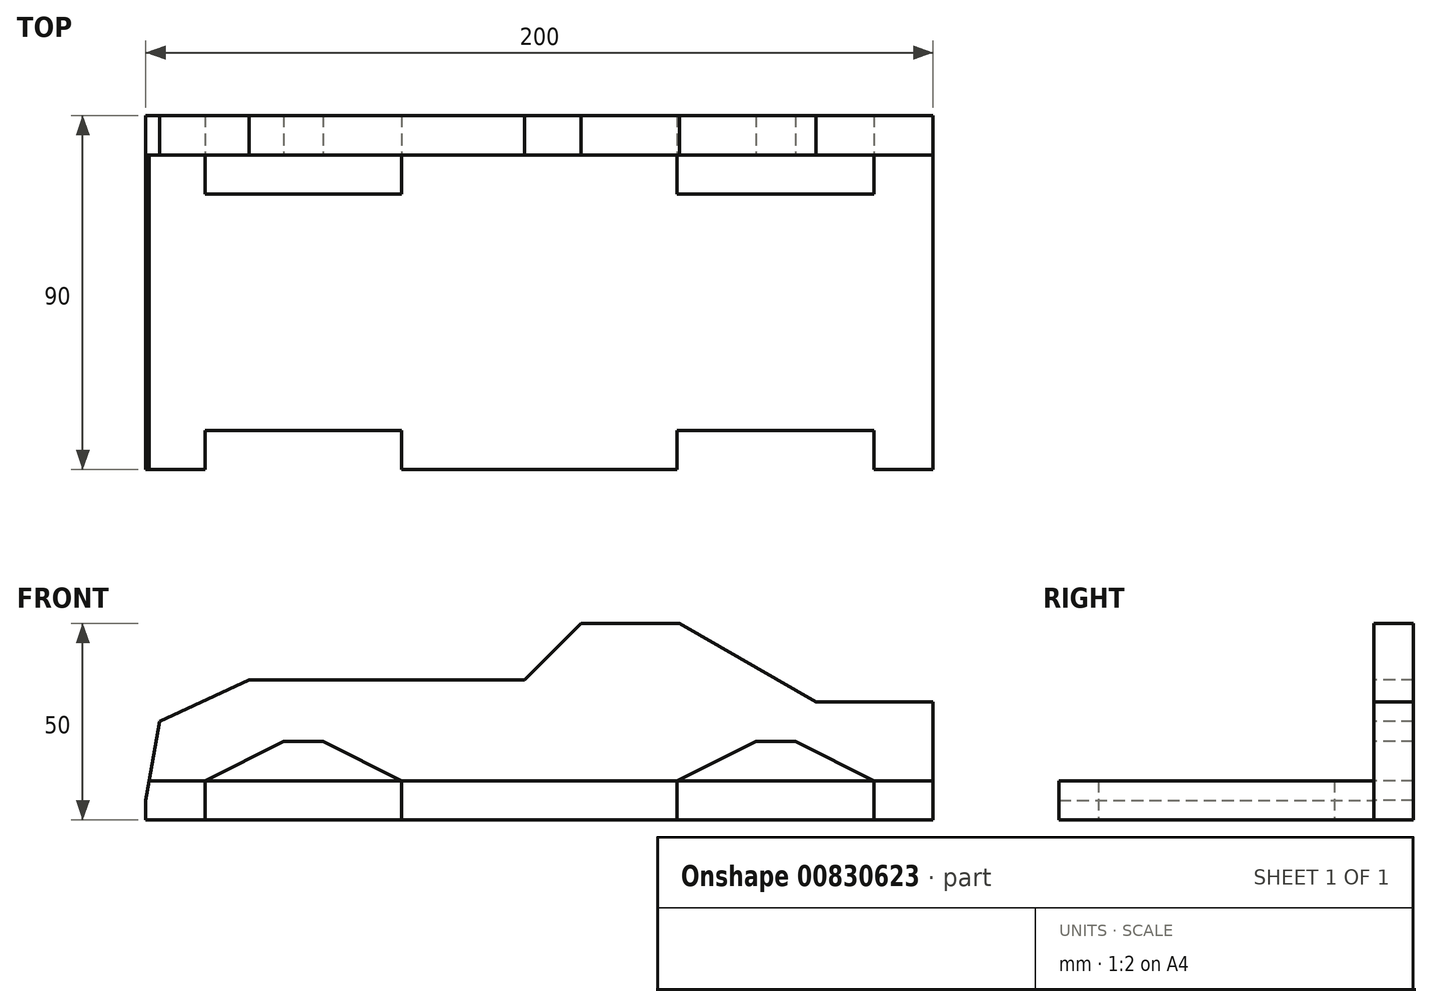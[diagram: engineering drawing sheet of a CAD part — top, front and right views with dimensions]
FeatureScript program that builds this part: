
annotation { "Feature Type Name" : "Feature", "Feature Type Description" : "" }
export const myFeature = defineFeature(function(context is Context, id is Id, definition is map)
    precondition{}
    {
        {
            var Q0;
            Q0=qCreatedBy(makeId("Front.planeOp"),FACE);
            var sketch = newSketch(context, id + "F0", { "sketchPlane" : qUnion([Q0])});
            skLineSegment(sketch, "E0.bottom", {"start": v(0, 0) * mm, "end": v(200, 0) * mm});
            skLineSegment(sketch, "E0.top", {"start": v(0, 50) * mm, "end": v(200, 50) * mm});
            skLineSegment(sketch, "E0.left", {"start": v(0, 0) * mm, "end": v(0, 50) * mm});
            skLineSegment(sketch, "E0.right", {"start": v(200, 0) * mm, "end": v(200, 50) * mm});
            skLineSegment(sketch, "E1.bottom", {"start": v(15, 0) * mm, "end": v(65, 0) * mm});
            skLineSegment(sketch, "E1.top", {"start": v(15, 10) * mm, "end": v(65, 10) * mm});
            skLineSegment(sketch, "E1.left", {"start": v(15, 0) * mm, "end": v(15, 10) * mm});
            skLineSegment(sketch, "E1.right", {"start": v(65, 0) * mm, "end": v(65, 10) * mm});
            skLineSegment(sketch, "E2.bottom", {"start": v(35, 10) * mm, "end": v(45, 10) * mm});
            skLineSegment(sketch, "E2.top", {"start": v(35, 20) * mm, "end": v(45, 20) * mm});
            skLineSegment(sketch, "E2.left", {"start": v(35, 10) * mm, "end": v(35, 20) * mm});
            skLineSegment(sketch, "E2.right", {"start": v(45, 10) * mm, "end": v(45, 20) * mm});
            skLineSegment(sketch, "E3", {"start": v(15, 10) * mm, "end": v(35, 20) * mm});
            skLineSegment(sketch, "E4", {"start": v(45, 20) * mm, "end": v(65, 10) * mm});
            skLineSegment(sketch, "E5", {"start": v(0, 5) * mm, "end": v(3.53, 25) * mm});
            skLineSegment(sketch, "E6", {"start": v(3.53, 25) * mm, "end": v(26.18, 35.57) * mm});
            skLineSegment(sketch, "E7", {"start": v(26.18, 35.57) * mm, "end": v(96.18, 35.57) * mm});
            skLineSegment(sketch, "E8", {"start": v(96.18, 35.57) * mm, "end": v(110.62, 50) * mm});
            skLineSegment(sketch, "E9", {"start": v(135.62, 50) * mm, "end": v(170.26, 30) * mm});
            skLineSegment(sketch, "E10", {"start": v(170.26, 30) * mm, "end": v(200, 30) * mm});
            skLineSegment(sketch, "E11", {"start": v(100, 0) * mm, "end": v(100, 17.97) * mm, "construction": true});
            skLineSegment(sketch, "E12.MirrorCS", {"start": v(185, 0) * mm, "end": v(185, 10) * mm});
            skLineSegment(sketch, "E13.MirrorCS", {"start": v(155, 10) * mm, "end": v(155, 20) * mm});
            skLineSegment(sketch, "E14.MirrorCS", {"start": v(135, 0) * mm, "end": v(135, 10) * mm});
            skLineSegment(sketch, "E15.MirrorCS", {"start": v(165, 10) * mm, "end": v(165, 20) * mm});
            skLineSegment(sketch, "E16.MirrorCS", {"start": v(165, 10) * mm, "end": v(155, 10) * mm});
            skLineSegment(sketch, "E17.MirrorCS", {"start": v(185, 10) * mm, "end": v(165, 20) * mm});
            skLineSegment(sketch, "E18.MirrorCS", {"start": v(185, 0) * mm, "end": v(135, 0) * mm});
            skLineSegment(sketch, "E19.MirrorCS", {"start": v(155, 20) * mm, "end": v(135, 10) * mm});
            skLineSegment(sketch, "E20.MirrorCS", {"start": v(165, 20) * mm, "end": v(155, 20) * mm});
            skLineSegment(sketch, "E21.MirrorCS", {"start": v(185, 10) * mm, "end": v(135, 10) * mm});
            skSolve(sketch);
        }
        {
            var Q0;
            Q0=qCreatedBy(makeId("Top.planeOp"),FACE);
            var sketch = newSketch(context, id + "F1", { "sketchPlane" : qUnion([Q0])});
            skLineSegment(sketch, "E22.bottom", {"start": v(0, 0) * mm, "end": v(200, 0) * mm});
            skLineSegment(sketch, "E22.top", {"start": v(0, -80) * mm, "end": v(200, -80) * mm});
            skLineSegment(sketch, "E22.left", {"start": v(0, 0) * mm, "end": v(0, -80) * mm});
            skLineSegment(sketch, "E22.right", {"start": v(200, 0) * mm, "end": v(200, -80) * mm});
            skLineSegment(sketch, "E23.0.1", {"start": v(185, 0) * mm, "end": v(165, 0) * mm});
            skLineSegment(sketch, "E23.0.2", {"start": v(165, 0) * mm, "end": v(155, 0) * mm});
            skLineSegment(sketch, "E23.0.3", {"start": v(155, 0) * mm, "end": v(135, 0) * mm});
            skLineSegment(sketch, "E23.0.5", {"start": v(135, 0) * mm, "end": v(185, 0) * mm});
            skLineSegment(sketch, "E24.0.0", {"start": v(45, 0) * mm, "end": v(35, 0) * mm});
            skLineSegment(sketch, "E24.0.1", {"start": v(35, 0) * mm, "end": v(15, 0) * mm});
            skLineSegment(sketch, "E24.0.3", {"start": v(15, 0) * mm, "end": v(65, 0) * mm});
            skLineSegment(sketch, "E24.0.5", {"start": v(65, 0) * mm, "end": v(45, 0) * mm});
            skLineSegment(sketch, "E25.bottom", {"start": v(185, 0) * mm, "end": v(135, 0) * mm});
            skLineSegment(sketch, "E25.top", {"start": v(185, -10) * mm, "end": v(135, -10) * mm});
            skLineSegment(sketch, "E25.left", {"start": v(185, 0) * mm, "end": v(185, -10) * mm});
            skLineSegment(sketch, "E25.right", {"start": v(135, 0) * mm, "end": v(135, -10) * mm});
            skLineSegment(sketch, "E26", {"start": v(100, 0) * mm, "end": v(100, -80) * mm, "construction": true});
            skLineSegment(sketch, "E27.MirrorCS", {"start": v(65, 0) * mm, "end": v(65, -10) * mm});
            skLineSegment(sketch, "E28.MirrorCS", {"start": v(15, -10) * mm, "end": v(65, -10) * mm});
            skLineSegment(sketch, "E29.MirrorCS", {"start": v(15, 0) * mm, "end": v(15, -10) * mm});
            skLineSegment(sketch, "E30", {"start": v(200, -40) * mm, "end": v(0, -40) * mm, "construction": true});
            skLineSegment(sketch, "E31.MirrorCS", {"start": v(185, -80) * mm, "end": v(185, -70) * mm});
            skLineSegment(sketch, "E32.MirrorCS", {"start": v(185, -70) * mm, "end": v(135, -70) * mm});
            skLineSegment(sketch, "E33.MirrorCS", {"start": v(135, -80) * mm, "end": v(135, -70) * mm});
            skLineSegment(sketch, "E34.MirrorCS", {"start": v(65, -80) * mm, "end": v(65, -70) * mm});
            skLineSegment(sketch, "E35.MirrorCS", {"start": v(15, -70) * mm, "end": v(65, -70) * mm});
            skLineSegment(sketch, "E36.MirrorCS", {"start": v(15, -80) * mm, "end": v(15, -70) * mm});
            skSolve(sketch);
        }
        {
            var Q0;
            {var subQ1=sQuery(id+"F1.wireOp",EDGE,"E22.left");Q0=makeQuery(id+"F1.imprint","IMPRINT",FACE,{"disambiguationData":[TD([[makeQuery(id+"F1.imprint","IMPRINT",EDGE,{"derivedFrom":subQ1}),1.0]])]});}
            extrude(context, id + "F2", {"entities" : qUnion([Q0]), "depth" : 10 * mm, "offsetDistance" : 25 * mm});
        }
        {
            var Q0;
            {var subQ9=sQuery(id+"F0.wireOp",EDGE,"E1.left");Q0=makeQuery(id+"F0.imprint","IMPRINT",FACE,{"disambiguationData":[TD([[makeQuery(id+"F0.imprint","IMPRINT",EDGE,{"derivedFrom":subQ9}),1.0]])]});}
            extrude(context, id + "F3", {"entities" : qUnion([Q0]), "oppositeDirection" : true, "depth" : 10 * mm, "offsetDistance" : 25 * mm});
        }
        {
            var Q0;
            Q0=makeQuery(id+"F2.opExtrude","CAP_EDGE",EDGE,{"disambiguationData":[OSD([sQuery(id+"F1.wireOp",EDGE,"E22.left")])],"isStart":false});
            chamfer(context, id + "F4", {"entities" : qUnion([Q0]), "chamferType" : ChamferType.OFFSET_ANGLE, "width" : 5 * mm, "oppositeDirection" : true, "angle" : 10 * degree, "tangentPropagation" : true});
        }
    });
